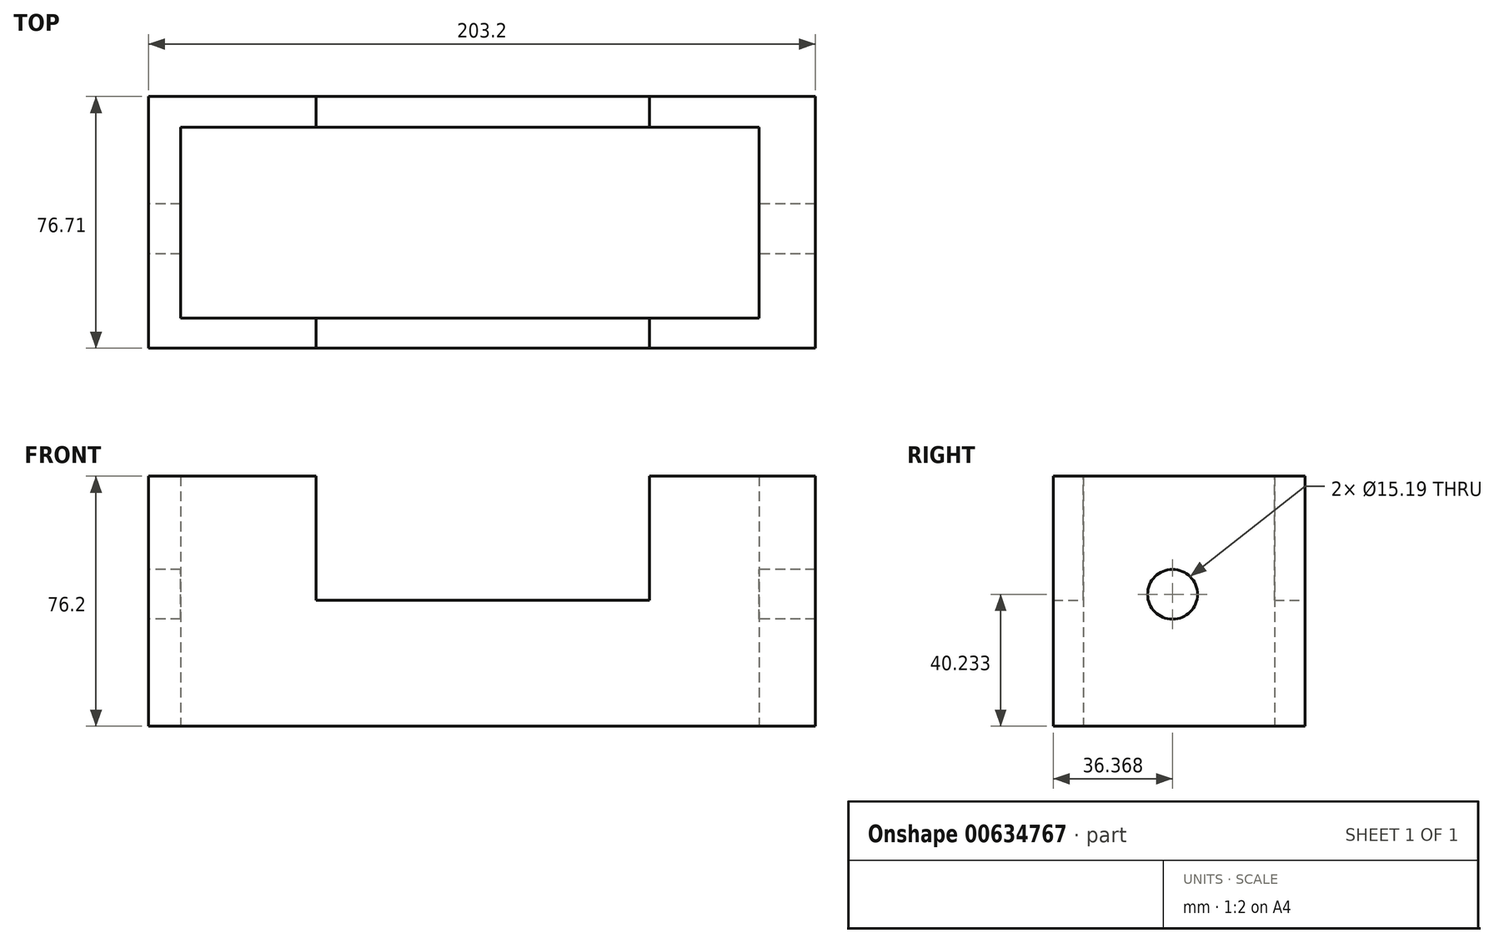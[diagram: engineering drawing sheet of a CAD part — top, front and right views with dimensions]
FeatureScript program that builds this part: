
annotation { "Feature Type Name" : "Feature", "Feature Type Description" : "" }
export const myFeature = defineFeature(function(context is Context, id is Id, definition is map)
    precondition{}
    {
        {
            var Q0;
            Q0=qCreatedBy(makeId("Front.planeOp"),FACE);
            var sketch = newSketch(context, id + "F0", { "sketchPlane" : qUnion([Q0])});
            skLineSegment(sketch, "E0", {"start": v(-52.68, 0) * mm, "end": v(150.52, 0) * mm});
            skLineSegment(sketch, "E1", {"start": v(150.52, 0) * mm, "end": v(150.52, 76.2) * mm});
            skLineSegment(sketch, "E2", {"start": v(150.52, 76.2) * mm, "end": v(-52.68, 76.2) * mm});
            skLineSegment(sketch, "E3", {"start": v(-52.68, 76.2) * mm, "end": v(-52.68, 0) * mm});
            skSolve(sketch);
        }
        {
            var Q0;
            Q0 = qSketchRegion(id + "F0", true);
            extrude(context, id + "F1", {"entities" : qUnion([Q0]), "depth" : 76.7 * mm, "offsetDistance" : 25.4 * mm});
        }
        {
            var Q0;
            Q0=qCreatedBy(makeId("Front.planeOp"),FACE);
            var sketch = newSketch(context, id + "F2", { "sketchPlane" : qUnion([Q0])});
            skLineSegment(sketch, "E4", {"start": v(-52.47, 0) * mm, "end": v(-1.67, 0) * mm});
            skLineSegment(sketch, "E5", {"start": v(-1.67, 0) * mm, "end": v(99.93, 0) * mm});
            skLineSegment(sketch, "E6", {"start": v(99.93, 0) * mm, "end": v(150.73, 0) * mm});
            skLineSegment(sketch, "E7", {"start": v(-52.47, 76.5) * mm, "end": v(-1.67, 76.5) * mm});
            skLineSegment(sketch, "E8", {"start": v(-1.67, 76.5) * mm, "end": v(99.93, 76.5) * mm});
            skPoint(sketch, "E8.endSnap0", {"position": v(-27.07, 76.5) * mm});
            skLineSegment(sketch, "E9", {"start": v(99.93, 76.5) * mm, "end": v(150.61, 76.5) * mm});
            skLineSegment(sketch, "E10", {"start": v(-1.67, 76.5) * mm, "end": v(-1.67, 38.4) * mm});
            skLineSegment(sketch, "E11", {"start": v(99.93, 76.5) * mm, "end": v(99.93, 38.4) * mm});
            skLineSegment(sketch, "E12", {"start": v(99.93, 38.4) * mm, "end": v(-1.67, 38.4) * mm});
            skSolve(sketch);
        }
        {
            var Q0;
            Q0=makeQuery(id+"F2.imprint","IMPRINT",FACE,{"disambiguationData":[TD([[makeQuery(id+"F2.imprint","IMPRINT",EDGE,{"derivedFrom":sQuery(id+"F2.wireOp",EDGE,"E8")}),-1.0]])]});
            extrude(context, id + "F3", {"entities" : qUnion([Q0]), "operationType" : NewBodyOperationType.REMOVE, "depth" : 116.33 * mm, "offsetDistance" : 25.4 * mm});
        }
        {
            var Q0;
            Q0=makeQuery(id+"F1.opExtrude","SWEPT_FACE",FACE,{"disambiguationData":[OSD([sQuery(id+"F0.wireOp",EDGE,"E3")])]});
            var sketch = newSketch(context, id + "F4", { "sketchPlane" : qUnion([Q0])});
            skCircle(sketch, "E13", {"center": v(40.34, 40.23) * mm, "radius": 7.6 * mm});
            skCircle(sketch, "E14", {"center": v(40.34, 40.23) * mm, "radius": 8.05 * mm});
            skSolve(sketch);
        }
        {
            var Q0;
            Q0=makeQuery(id+"F4.imprint","IMPRINT",FACE,{"disambiguationData":[TD([[makeQuery(id+"F4.imprint","IMPRINT",EDGE,{"derivedFrom":sQuery(id+"F4.wireOp",EDGE,"E13")}),1.0]])]});
            extrude(context, id + "F5", {"entities" : qUnion([Q0]), "operationType" : NewBodyOperationType.REMOVE, "endBound" : BoundingType.SYMMETRIC, "oppositeDirection" : true, "depth" : 469.9 * mm, "offsetDistance" : 25.4 * mm});
        }
        {
            var Q0;
            Q0=makeQuery(id+"F1.opExtrude","SWEPT_FACE",FACE,{"disambiguationData":[OSD([sQuery(id+"F0.wireOp",EDGE,"E0")])]});
            var sketch = newSketch(context, id + "F6", { "sketchPlane" : qUnion([Q0])});
            skLineSegment(sketch, "E15.bottom", {"start": v(-42.92, 9.3) * mm, "end": v(133.33, 9.3) * mm});
            skLineSegment(sketch, "E15.top", {"start": v(-42.92, 67.55) * mm, "end": v(133.33, 67.55) * mm});
            skLineSegment(sketch, "E15.left", {"start": v(-42.92, 9.3) * mm, "end": v(-42.92, 67.55) * mm});
            skLineSegment(sketch, "E15.right", {"start": v(133.33, 9.3) * mm, "end": v(133.33, 67.55) * mm});
            skSolve(sketch);
        }
        {
            var Q0;
            Q0 = qSketchRegion(id + "F6", true);
            extrude(context, id + "F7", {"entities" : qUnion([Q0]), "operationType" : NewBodyOperationType.REMOVE, "oppositeDirection" : true, "depth" : 93.47 * mm, "offsetDistance" : 25.4 * mm});
        }
    });
